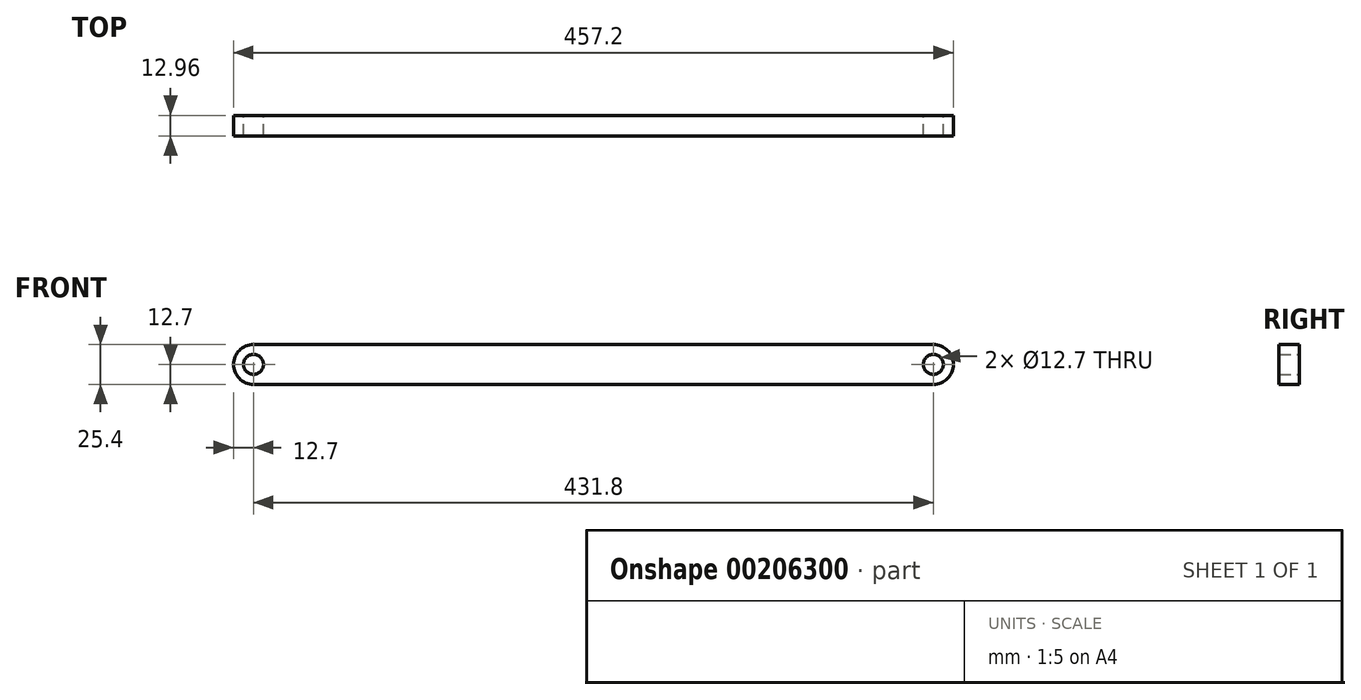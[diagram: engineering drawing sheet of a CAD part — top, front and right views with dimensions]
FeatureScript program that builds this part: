
annotation { "Feature Type Name" : "Feature", "Feature Type Description" : "" }
export const myFeature = defineFeature(function(context is Context, id is Id, definition is map)
    precondition{}
    {
        {
            var Q0;
            Q0=qCreatedBy(makeId("Front.planeOp"),FACE);
            var sketch = newSketch(context, id + "F0", { "sketchPlane" : qUnion([Q0])});
            skLineSegment(sketch, "E0", {"start": v(-215.9, 0) * mm, "end": v(215.9, 0) * mm, "construction": true});
            skArc(sketch, "E1.0.startCap", {"start": v(-215.9, -12.7) * mm, "mid": v(-228.6, 0) * mm, "end": v(-215.9, 12.7) * mm});
            skArc(sketch, "E1.0.endCap", {"start": v(215.9, 12.7) * mm, "mid": v(228.6, 0) * mm, "end": v(215.9, -12.7) * mm});
            skLineSegment(sketch, "E1.0.left", {"start": v(-215.9, 12.7) * mm, "end": v(215.9, 12.7) * mm});
            skLineSegment(sketch, "E1.0.right", {"start": v(-215.9, -12.7) * mm, "end": v(215.9, -12.7) * mm});
            skCircle(sketch, "E2", {"center": v(-215.9, 0) * mm, "radius": 6.35 * mm});
            skCircle(sketch, "E3", {"center": v(215.9, 0) * mm, "radius": 6.35 * mm});
            skSolve(sketch);
        }
        {
            var Q0;
            Q0 = qSketchRegion(id + "F0", true);
            extrude(context, id + "F1", {"entities" : qUnion([Q0]), "endBound" : BoundingType.SYMMETRIC, "depth" : 12.95 * mm});
        }
    });
